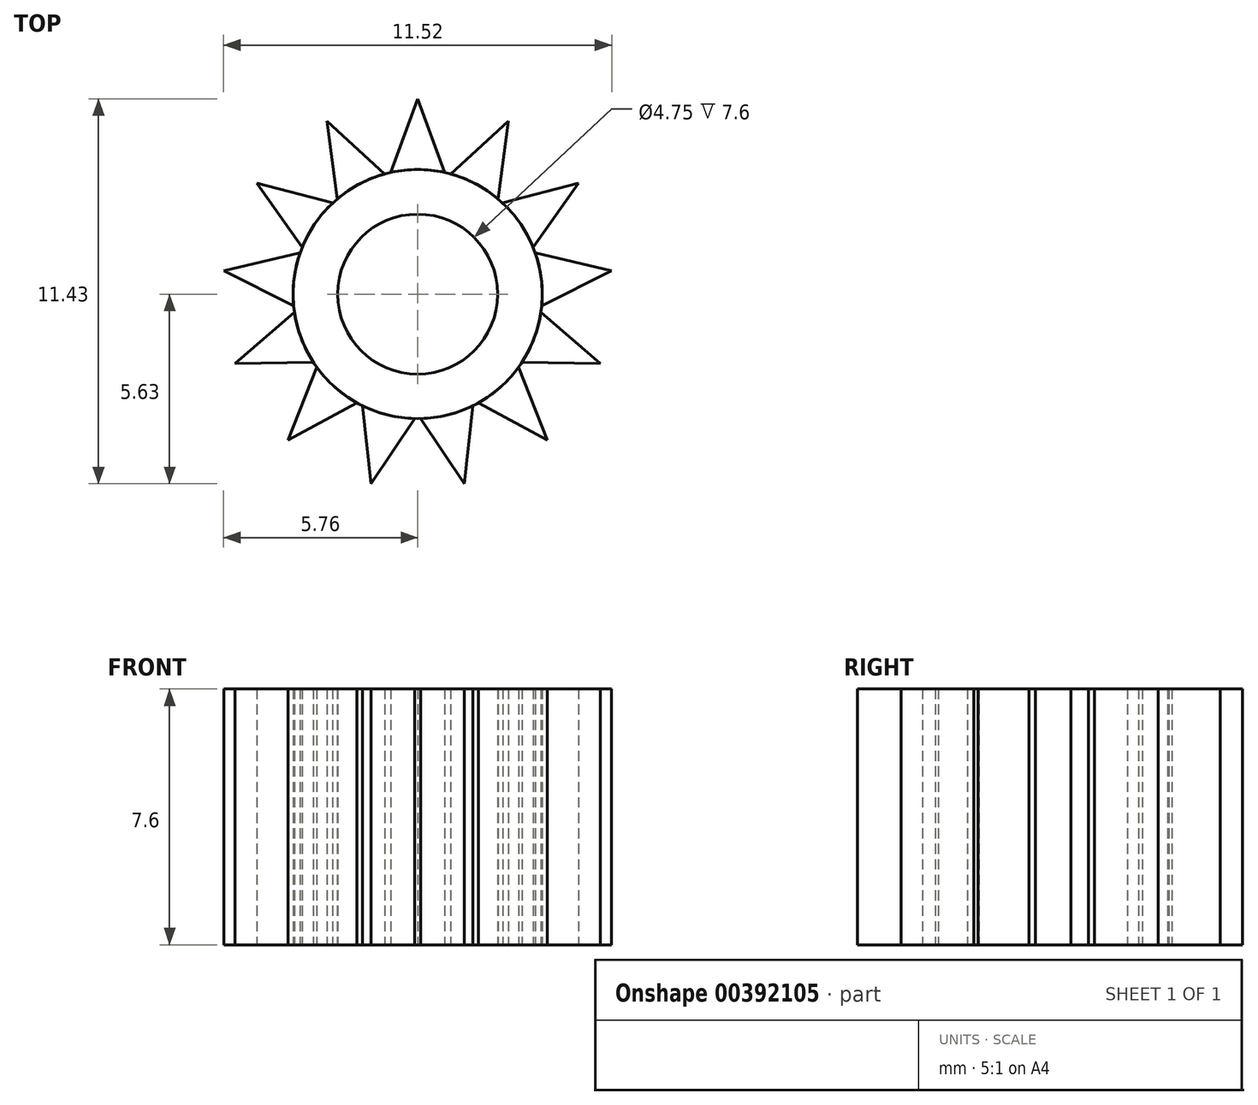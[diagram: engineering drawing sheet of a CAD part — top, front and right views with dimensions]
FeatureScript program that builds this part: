
annotation { "Feature Type Name" : "Feature", "Feature Type Description" : "" }
export const myFeature = defineFeature(function(context is Context, id is Id, definition is map)
    precondition{}
    {
        {
            var Q0;
            Q0=qCreatedBy(makeId("Top.planeOp"),FACE);
            var sketch = newSketch(context, id + "F0", { "sketchPlane" : qUnion([Q0])});
            skCircle(sketch, "E0", {"center": v(0, 0) * mm, "radius": 3.7 * mm});
            skLineSegment(sketch, "E1", {"start": v(0, 3.7) * mm, "end": v(0, 5.8) * mm});
            skLineSegment(sketch, "E2", {"start": v(0, 5.8) * mm, "end": v(-0.8, 3.61) * mm});
            skLineSegment(sketch, "E3", {"start": v(0, 5.8) * mm, "end": v(0.8, 3.61) * mm});
            skCircle(sketch, "E4", {"center": v(0, 0) * mm, "radius": 2.38 * mm});
            skSolve(sketch);
        }
        {
            var Q0;
            {var subQ0=sQuery(id+"F0.wireOp",EDGE,"E1");Q0=makeQuery(id+"F0.imprint","IMPRINT",FACE,{"disambiguationData":[TD([[makeQuery(id+"F0.imprint","IMPRINT",EDGE,{"derivedFrom":subQ0}),1.0]])]});}
            var Q1;
            {var subQ0=sQuery(id+"F0.wireOp",EDGE,"E1");Q1=makeQuery(id+"F0.imprint","IMPRINT",FACE,{"disambiguationData":[TD([[makeQuery(id+"F0.imprint","IMPRINT",EDGE,{"derivedFrom":subQ0}),-1.0]])]});}
            extrude(context, id + "F1", {"entities" : qUnion([Q0, Q1]), "depth" : 7.6 * mm});
        }
        {
            var Q0;
            Q0=qCreatedBy(makeId("Right.planeOp"),FACE);
            var sketch = newSketch(context, id + "F2", { "sketchPlane" : qUnion([Q0])});
            skLineSegment(sketch, "E5", {"start": v(0, 0) * mm, "end": v(0, 14.49) * mm});
            skSolve(sketch);
        }
        {
            var Q0;
            Q0=makeQuery(id+"F1.opExtrude","SWEPT_BODY",BODY,{"disambiguationData":[OSD([sQuery(id+"F0.wireOp",EDGE,"E0"),sQuery(id+"F0.wireOp",EDGE,"E2"),sQuery(id+"F0.wireOp",EDGE,"E3")])]});
            var Q1;
            Q1=sQuery(id+"F2.wireOp",EDGE,"E5");
            circularPattern(context, id + "F3", {"entities" : qUnion([Q0]), "axis" : qUnion([Q1]), "angle" : 360 * degree, "instanceCount" : 13, "equalSpace" : true});
        }
        {
            var Q0;
            {var subQ7=sQuery(id+"F0.wireOp",EDGE,"E0");var subQ8=makeQuery(id+"F0.imprint","INTERSECT",VERTEX,{"derivedFrom":[subQ7,sQuery(id+"F0.wireOp",EDGE,"E1")]});Q0=makeQuery(id+"F0.imprint","IMPRINT",FACE,{"disambiguationData":[TD([[makeQuery(id+"F0.imprint","IMPRINT",EDGE,{"disambiguationData":[TD([[subQ8,1.0]])],"derivedFrom":subQ7}),1.0]])]});}
            extrude(context, id + "F4", {"entities" : qUnion([Q0]), "depth" : 7.6 * mm});
        }
    });
